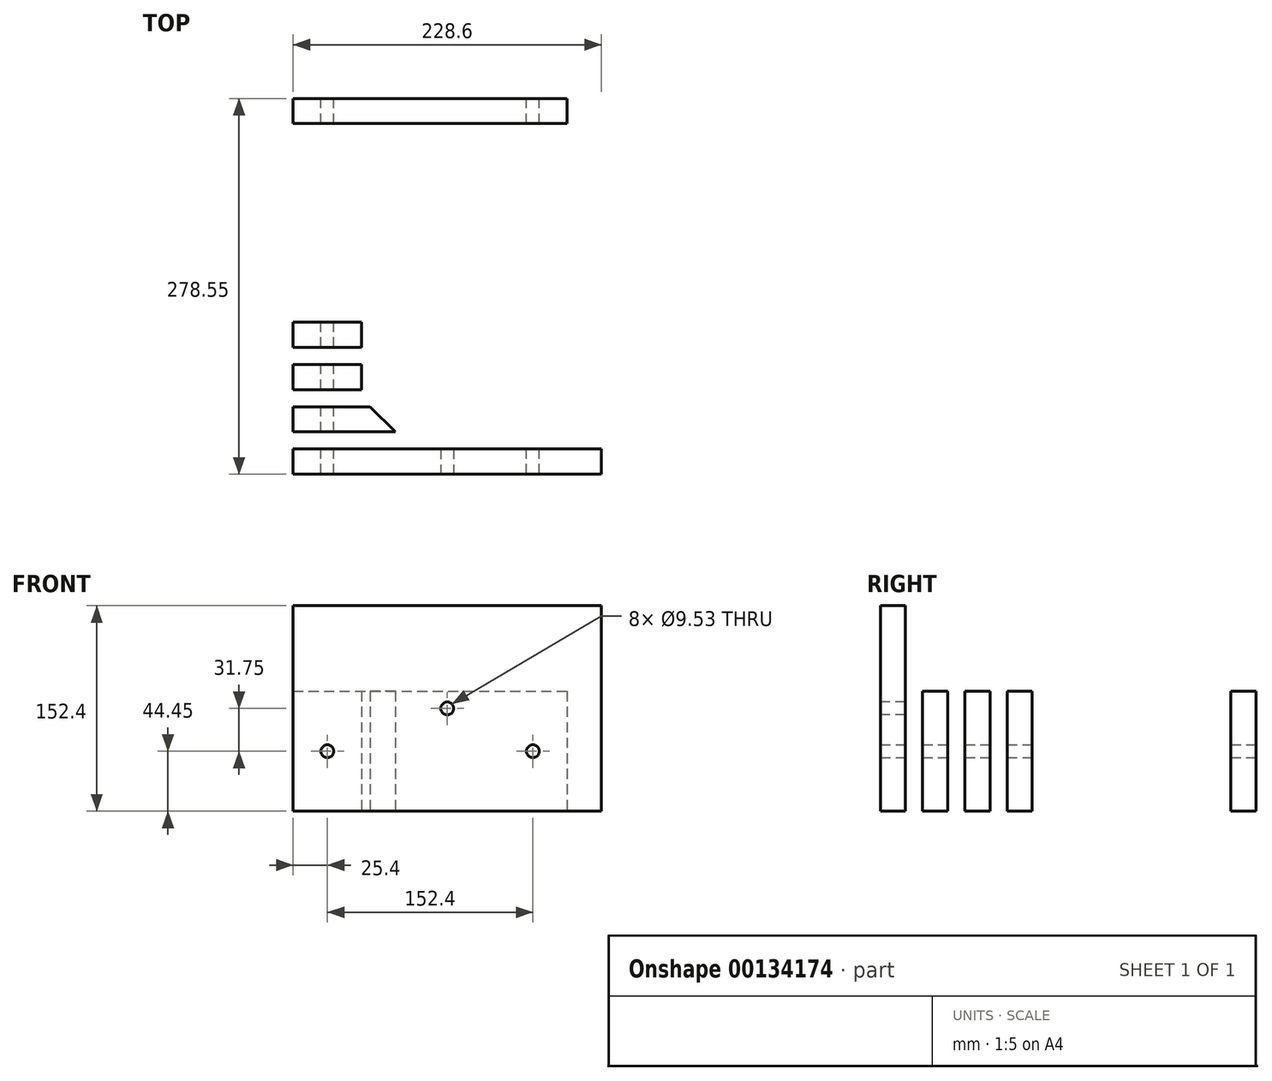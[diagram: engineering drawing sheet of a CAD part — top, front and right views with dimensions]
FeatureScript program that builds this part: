
annotation { "Feature Type Name" : "Feature", "Feature Type Description" : "" }
export const myFeature = defineFeature(function(context is Context, id is Id, definition is map)
    precondition{}
    {
        {
            var Q0;
            Q0=qCreatedBy(makeId("Top.planeOp"),FACE);
            var sketch = newSketch(context, id + "F0", { "sketchPlane" : qUnion([Q0])});
            skLineSegment(sketch, "E0.bottom", {"start": v(-101.6, 62.69) * mm, "end": v(-44.45, 62.69) * mm});
            skLineSegment(sketch, "E0.top", {"start": v(-101.6, 44.04) * mm, "end": v(-25.8, 44.04) * mm});
            skLineSegment(sketch, "E0.left", {"start": v(-101.6, 62.69) * mm, "end": v(-101.6, 44.04) * mm});
            skLineSegment(sketch, "E1.bottom", {"start": v(-101.6, 75.39) * mm, "end": v(-50.8, 75.39) * mm});
            skLineSegment(sketch, "E1.top", {"start": v(-101.6, 94.03) * mm, "end": v(-50.8, 94.03) * mm});
            skLineSegment(sketch, "E1.left", {"start": v(-101.6, 75.39) * mm, "end": v(-101.6, 94.03) * mm});
            skLineSegment(sketch, "E1.right", {"start": v(-50.8, 75.39) * mm, "end": v(-50.8, 94.03) * mm});
            skLineSegment(sketch, "E2.bottom", {"start": v(-101.6, 106.73) * mm, "end": v(-50.8, 106.73) * mm});
            skLineSegment(sketch, "E2.top", {"start": v(-101.6, 125.37) * mm, "end": v(-50.8, 125.37) * mm});
            skLineSegment(sketch, "E2.left", {"start": v(-101.6, 106.73) * mm, "end": v(-101.6, 125.37) * mm});
            skLineSegment(sketch, "E2.right", {"start": v(-50.8, 106.73) * mm, "end": v(-50.8, 125.37) * mm});
            skLineSegment(sketch, "E3", {"start": v(-25.8, 44.04) * mm, "end": v(-44.45, 62.69) * mm});
            skLineSegment(sketch, "E4.bottom", {"start": v(-101.6, 272.6) * mm, "end": v(101.6, 272.6) * mm});
            skLineSegment(sketch, "E4.top", {"start": v(-101.6, 291.25) * mm, "end": v(101.6, 291.25) * mm});
            skLineSegment(sketch, "E4.left", {"start": v(-101.6, 272.6) * mm, "end": v(-101.6, 291.25) * mm});
            skLineSegment(sketch, "E4.right", {"start": v(101.6, 272.6) * mm, "end": v(101.6, 291.25) * mm});
            skPoint(sketch, "E5.start.orphan", {"position": v(0, 57.42) * mm});
            skPoint(sketch, "E6.MirrorCS.end.orphan", {"position": v(44.45, 26.31) * mm});
            skLineSegment(sketch, "E7.bottom", {"start": v(-101.6, 31.34) * mm, "end": v(127, 31.34) * mm});
            skLineSegment(sketch, "E7.top", {"start": v(-101.6, 12.7) * mm, "end": v(127, 12.7) * mm});
            skLineSegment(sketch, "E7.left", {"start": v(-101.6, 31.34) * mm, "end": v(-101.6, 12.7) * mm});
            skLineSegment(sketch, "E7.right", {"start": v(127, 31.34) * mm, "end": v(127, 12.7) * mm});
            skPoint(sketch, "E8.MirrorCS.start.orphan", {"position": v(-101.6, 255.86) * mm});
            skPoint(sketch, "E9.MirrorCS.start.orphan", {"position": v(101.6, 255.86) * mm});
            skSolve(sketch);
        }
        {
            var Q0;
            Q0=makeQuery(id+"F0.imprint","IMPRINT",FACE,{"disambiguationData":[TD([[makeQuery(id+"F0.imprint","IMPRINT",EDGE,{"derivedFrom":sQuery(id+"F0.wireOp",EDGE,"E7.bottom")}),-1.0]])]});
            extrude(context, id + "F4", {"entities" : qUnion([Q0]), "depth" : 152.4 * mm});
        }
        {
            var Q0;
            Q0=makeQuery(id+"F4.opExtrude","SWEPT_FACE",FACE,{"disambiguationData":[OSD([sQuery(id+"F0.wireOp",EDGE,"E7.top")])]});
            var sketch = newSketch(context, id + "F1", { "sketchPlane" : qUnion([Q0])});
            skCircle(sketch, "E10", {"center": v(12.7, 76.2) * mm, "radius": 4.76 * mm});
            skPoint(sketch, "E10.centerSnap0", {"position": v(12.7, 152.4) * mm});
            skSolve(sketch);
        }
        {
            var Q0;
            Q0=makeQuery(id+"F1.imprint","IMPRINT",FACE,{"disambiguationData":[TD([[makeQuery(id+"F1.imprint","IMPRINT",EDGE,{"derivedFrom":sQuery(id+"F1.wireOp",EDGE,"E10")}),1.0]])]});
            extrude(context, id + "F2", {"entities" : qUnion([Q0]), "operationType" : NewBodyOperationType.REMOVE, "oppositeDirection" : true, "depth" : 25.4 * mm});
        }
        {
            var Q0;
            Q0=makeQuery(id+"F0.imprint","IMPRINT",FACE,{"disambiguationData":[TD([[makeQuery(id+"F0.imprint","IMPRINT",EDGE,{"derivedFrom":sQuery(id+"F0.wireOp",EDGE,"E0.bottom")}),-1.0]])]});
            var Q1;
            Q1=makeQuery(id+"F0.imprint","IMPRINT",FACE,{"disambiguationData":[TD([[makeQuery(id+"F0.imprint","IMPRINT",EDGE,{"derivedFrom":sQuery(id+"F0.wireOp",EDGE,"E1.bottom")}),1.0]])]});
            var Q2;
            Q2=makeQuery(id+"F0.imprint","IMPRINT",FACE,{"disambiguationData":[TD([[makeQuery(id+"F0.imprint","IMPRINT",EDGE,{"derivedFrom":sQuery(id+"F0.wireOp",EDGE,"E2.bottom")}),1.0]])]});
            var Q3;
            Q3=makeQuery(id+"F0.imprint","IMPRINT",FACE,{"disambiguationData":[TD([[makeQuery(id+"F0.imprint","IMPRINT",EDGE,{"derivedFrom":sQuery(id+"F0.wireOp",EDGE,"E4.bottom")}),1.0]])]});
            extrude(context, id + "F3", {"entities" : qUnion([Q0, Q1, Q2, Q3]), "depth" : 88.9 * mm});
        }
        {
            var Q0;
            Q0=makeQuery(id+"F3.opExtrude","SWEPT_FACE",FACE,{"disambiguationData":[OSD([sQuery(id+"F0.wireOp",EDGE,"E4.top")])]});
            var sketch = newSketch(context, id + "F5", { "sketchPlane" : qUnion([Q0])});
            skCircle(sketch, "E11", {"center": v(76.2, 44.45) * mm, "radius": 4.76 * mm});
            skPoint(sketch, "E11.centerSnap0", {"position": v(101.6, 44.45) * mm});
            skCircle(sketch, "E12", {"center": v(-76.2, 44.45) * mm, "radius": 4.76 * mm});
            skPoint(sketch, "E12.centerSnap0", {"position": v(-101.6, 44.45) * mm});
            skSolve(sketch);
        }
        {
            var Q0;
            Q0=makeQuery(id+"F5.imprint","IMPRINT",FACE,{"disambiguationData":[TD([[makeQuery(id+"F5.imprint","IMPRINT",EDGE,{"derivedFrom":sQuery(id+"F5.wireOp",EDGE,"E11")}),1.0]])]});
            var Q1;
            Q1=makeQuery(id+"F5.imprint","IMPRINT",FACE,{"disambiguationData":[TD([[makeQuery(id+"F5.imprint","IMPRINT",EDGE,{"derivedFrom":sQuery(id+"F5.wireOp",EDGE,"E12")}),1.0]])]});
            extrude(context, id + "F6", {"entities" : qUnion([Q0, Q1]), "operationType" : NewBodyOperationType.REMOVE, "endBound" : BoundingType.THROUGH_ALL, "oppositeDirection" : true, "depth" : 25.4 * mm});
        }
    });
